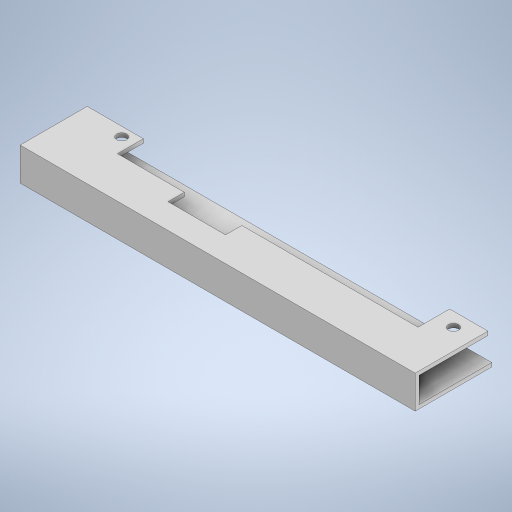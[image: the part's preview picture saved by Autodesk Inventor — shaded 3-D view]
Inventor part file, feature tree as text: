
AUTODESK INVENTOR PART (.ipt)
format: ipt  version: 2024 (Build 280153000, 153)  size: 280,064 bytes
history: native  units: in
note: dims shown in document units (in); Inventor stores cm internally (conversion verified against a paired STEP export)
features: extrude x4, sketch x1
ambient origin geometry x8: Origin, YZ Plane, XZ Plane, XY Plane, X Axis, Y Axis, Z Axis, Center Point
bodies: Solid1 (feature_tree)
feature tree (5):
  sketch  "Sketch1"  dims[d0=0.1043in d1=0.1043in d2=4.0591in d3=0.5768in d4=0.3937in d5=0.7087in d6=0.6496in d7=0.5541in d8=0.4498in d9=0.3839in d10=0.564in d11=0.2096in d12=0.0394in d13=0.0in d14=0.0394in d15=0.2992in d16=0.0in d17=0.0394in d18=0.748in d19=0.0in d21=0.5906in d23=0.0787in d24=0.0in d26=0.2559in d28=1.811in]
  extrude  "Extrusion1"  Depth=1.811in
  extrude  "Extrusion2"  Depth=4.0591in
  extrude  "Extrusion3"  Depth=0.5768in
  extrude  "Extrusion4"  Depth=0.3937in
